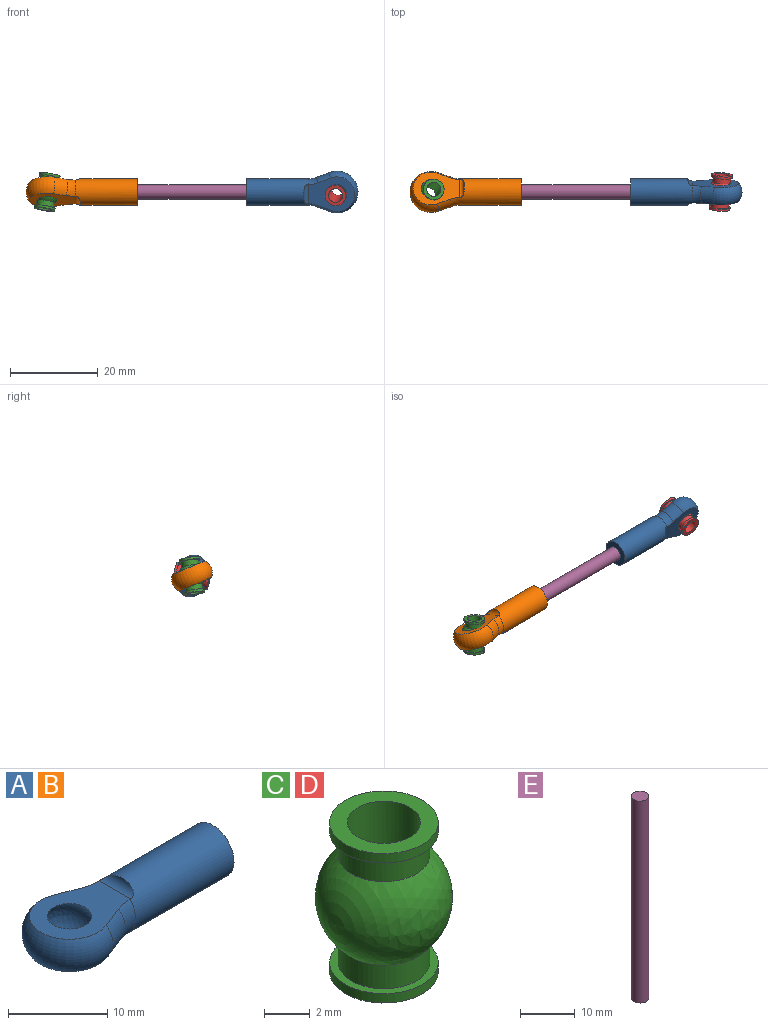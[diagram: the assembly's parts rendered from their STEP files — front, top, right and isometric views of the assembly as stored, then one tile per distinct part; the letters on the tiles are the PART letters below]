
ASSEMBLY  parts=5 mates=4
PART A: 14 faces, bbox 24.5x8.9x6 mm
  f0: cylinder r=3mm len=14.06mm, axis (1,0,0), area 255.6mm2, adj f3,f4,f6,f7,f8,f9,f10
  f1: cylinder r=3mm len=4mm, axis (0.93,-0.36,0), area 13.5mm2, adj f3,f5,f7,f8
  f2: cylinder r=3mm len=4mm, axis (-0.93,-0.36,0), area 13.5mm2, adj f4,f5,f7,f8
  f3: torus R=8mm, axis (0,0,1), area 8.6mm2, adj f0,f1,f7,f8
  f4: torus R=8mm, axis (0,0,1), area 8.6mm2, adj f0,f2,f7,f8
  f5: torus R=1.8mm, axis (0,0,1), area 77.3mm2, adj f1,f2,f7,f8
  f6: plane 6x6mm, normal (1,0,0), area 20.2mm2, adj f0,f11
  f7: plane 10.54x8.07mm, normal (0,0,-1), area 50mm2, adj f0,f1,f2,f3,f4,f5,f10,f13
  f8: plane 10.54x8.07mm, normal (0,0,1), area 50mm2, adj f0,f1,f2,f3,f4,f5,f9,f13
  f9: cylinder r=1mm len=4.47mm, axis (0,1,0), area 5.5mm2, adj f0,f8
  f10: cylinder r=1mm len=4.47mm, axis (0,-1,0), area 5.5mm2, adj f0,f7
  f11: cylinder r=1.6mm len=10mm, axis (1,0,0), area 100.5mm2, adj f6,f12
  f12: plane 3.2x3.2mm, normal (1,0,0), area 8mm2, adj f11
  f13: sphere r=3mm, area 75.4mm2, adj f7,f8
PART B: same geometry as A
PART C: 10 faces, bbox 6x6x8 mm
  f0: cylinder r=2mm len=4mm, axis (0,0,-1), area 15.9mm2, adj f1,f8
  f1: sphere r=3mm, area 84.3mm2, adj f0,f2
  f2: cylinder r=2mm len=4mm, axis (0,0,-1), area 15.9mm2, adj f1,f5
  f3: cylinder r=2.38mm len=4.75mm, axis (0,0,-1), area 7.5mm2, adj f4,f5
  f4: plane 4.75x4.75mm, normal (0,0,1), area 9.7mm2, adj f3,f9
  f5: plane 4.75x4.75mm, normal (0,0,-1), area 5.2mm2, adj f2,f3
  f6: cylinder r=2.38mm len=4.75mm, axis (0,0,1), area 7.5mm2, adj f7,f8
  f7: plane 4.75x4.75mm, normal (0,0,-1), area 9.7mm2, adj f6,f9
  f8: plane 4.75x4.75mm, normal (0,0,1), area 5.2mm2, adj f0,f6
  f9: cylinder r=1.6mm len=8mm, axis (0,0,-1), area 80.4mm2, adj f4,f7
PART D: same geometry as C
PART E: 3 faces, bbox 3.2x3.2x45 mm
  f0: cylinder r=1.6mm len=45mm, axis (0,0,-1), area 452.4mm2, adj f1,f2
  f1: plane 3.2x3.2mm, normal (0,0,1), area 8mm2, adj f0
  f2: plane 3.2x3.2mm, normal (0,0,-1), area 8mm2, adj f0
PLACE A rot(axis=(0,-0.79,0.62),180deg) t=(31.51,3.16,4.91)mm
PLACE B rot(axis=(-1,0,0),23.1deg) t=(6.65,-2.96,-0.32)mm
PLACE C rot(axis=(-0.17,0.31,0.93),34.7deg) t=(-13.85,0.98,1.27)mm
PLACE D rot(axis=(-0.98,0.15,0.09),78.6deg) t=(52.01,0.98,1.27)mm
PLACE E rot(axis=(0.7,0.16,0.7),161.9deg) t=(-6.02,0.98,1.27)mm fixed
MATE ball A.f5 <-> D.f3  axis (0,-0.97,-0.24) through (52.01,0.98,1.27)mm
MATE cylindrical E.f0 <-> B.f0  axis (-1,0,0) through (16.48,0.98,1.27)mm
MATE ball B.f5 <-> C.f3  axis (0,0.39,0.92) through (-13.85,0.98,1.27)mm
MATE cylindrical E.f0 <-> A.f0  axis (-1,0,0) through (16.48,0.98,1.27)mm
